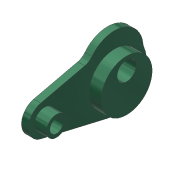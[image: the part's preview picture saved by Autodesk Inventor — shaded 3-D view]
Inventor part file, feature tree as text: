
AUTODESK INVENTOR PART (.ipt)
format: ipt  version: 2019.4 (Build 234330000, 330)  size: 139,776 bytes
history: native  units: mm
features: sketch x4, extrude x2, hole x2, other x1
ambient origin geometry x8: Origin, YZ Plane, XZ Plane, XY Plane, X Axis, Y Axis, Z Axis, Center Point
bodies: Body1 (feature_tree)
feature tree (9):
  other  "ソリッド1"
  extrude  "押し出し1"  Depth=11.0mm
  extrude  "押し出し2"  Depth=8.0mm
  sketch  "スケッチ3"
  sketch  "スケッチ4"
  hole  "穴3"  [1 undecoded]
  hole  "穴4"  [1 undecoded]
  sketch  "スケッチ1"
  sketch  "スケッチ2"
note: 2 required parameter values undecoded (feature->parameter linkage not recoverable at this tier; creation-order binding heuristic only, values carry confidence <= 0.55)
